# Revit family: Hager-Univers-IP54-D205-H1950-Cl.I-Encl-CH-it
name_source: partatom
category: Equipement électrique
units: mm (PartAtom-declared; Revit-internal decimal feet)

## family parameters
Configuration du panneau = Deux colonnes, circuits au sein
Cote de connecteur circulaire = Utiliser le diamètre
Couper avec des vides une fois chargée = Non
Hôte = Face
Partagée = Non
Point de calcul de pièce = Non
Type d'élément = Tableau de raccordement

## types (4) — shared parameters
Commentaires du type = Univers
EF000003 - Tipo di montaggio = EV012274 - montaggio a pavimento
EF000007 - colore = EV000202 - bianco
EF000040 - Altezza = 1950 mm  [stored 6.39764 ft]
EF000049 - profondità = 205 mm  [stored 0.672572 ft]
EF000116 - numero RAL = 9010
EF000118 - con piastra di montaggio = Non
EF000266 - numero di file = 12
EF000339 - tipo di copertura = EV001012 - coperchio
EF001088 - possibilità di applicazione = Oui
EF001131 - profondità interna = 205 mm  [stored 0.672572 ft]
EF001596 - Attacco Lampada = EV000179 - acciaio
EF001613 - Integrità del circuito = EV000494 - senza
EF003532 - adatto per uso esterno = Non
EF004293 - resistenza agli urti = EV006815 - IK09
EF005474 - grado di protezione (IP) = EV006419 - IP54
EF006244 - coperchio/porta trasparente = Non
EF006306 - con serratura = Non
EF007800 - adatto per parafulmine = Non
EF009170 - spessore materiale scatola = 1 mm  [stored 0.00328084 ft]
EF009171 - spessore materiale porta/coperchio = 1 mm  [stored 0.00328084 ft]
EF009212 - esecuzione coperchio = EV000116 - chiuso
EF015940 - Coprire con rilascio di sovrapressione = Non
Fabricant = Hager
HG000002 - Con porta = Oui
HG000003 - Gamma = Univers
HG000006 - Ad incasso = Non
HG000023 - Custodia a doppia sezione = Non
HG000024 - Altezza della sezione inferiore = 800 mm  [stored 2.62467 ft]
HG000026 - A pavimento = Oui
HG000027 - Altezza dello zoccolo = 100 mm  [stored 0.328084 ft]
zero-valued in all types: EF000218 - profondità di incasso, Elévation par défaut

## per-type parameters (varying)
| type | EF000008 - Larghezza | EF000437 - numero di ingressi per conduttori | EF002950 - Numero moduli DIN | EF004427 - numero di moduli | EF004464 - tipo di porta | EF008873 - corrente nominale (In) | EF009554 - numero delle aperture per la piastra della flangia | HG000004 - Codice produttore | HG000009 - Porta doppia a battente | HG000010 - Porte asimmetriche |
| montaggio a pavimento IP54 L1300 A1950 P205  - FP25TW2 | 1300 mm  [stored 4.26509 ft] | 10 | 60 | 720 | EV003602 - doppio | 400 A | 10 | FP25TW2 | Oui | Oui |
| montaggio a pavimento IP54 L300 A1950 P205  - FP21TW2 | 300 mm | 2 | 12 | 144 | EV002646 - singolo | 250 A | 2 | FP21TW2 | Non | Non |
| montaggio a pavimento IP54 L550 A1950 P205  - FP22TW2 | 550 mm | 4 | 24 | 288 | EV002646 - singolo | 400 A | 4 | FP22TW2 | Non | Non |
| montaggio a pavimento IP54 L800 A1950 P205  - FP23TW2 | 800 mm  [stored 2.62467 ft] | 6 | 36 | 432 | EV002646 - singolo | 400 A | 6 | FP23TW2 | Oui | Oui |

note: [stored X ft] marks values corroborated as IEEE doubles in the binary element streams (Revit-internal decimal feet)

## geometry (parser evidence)
native form markers: Sweep x9
no freeform markers — native parametric forms only
